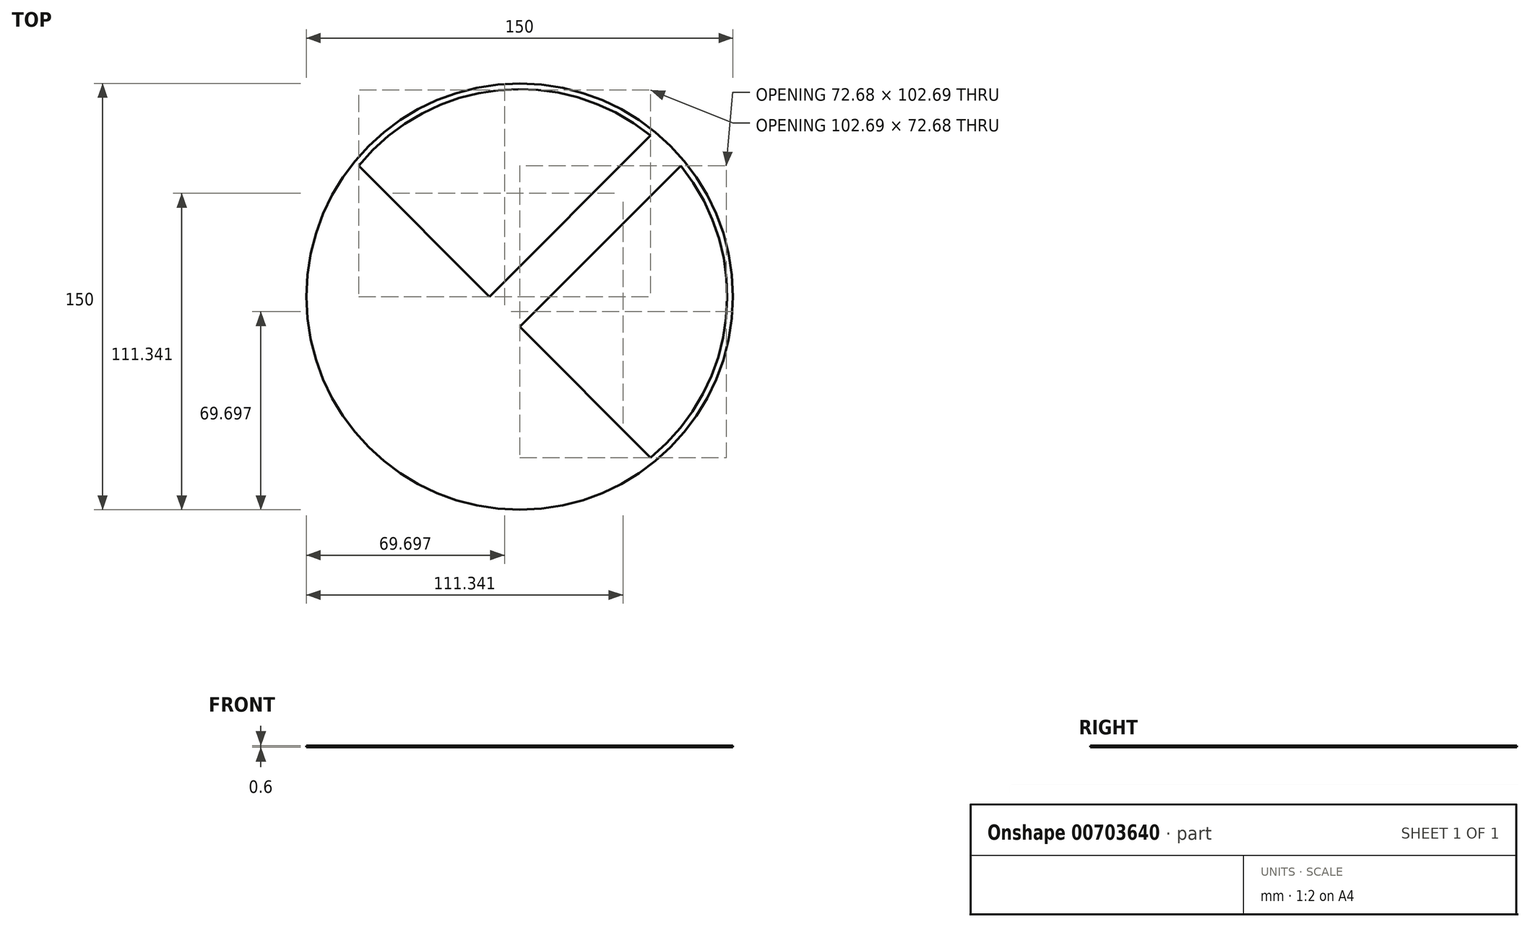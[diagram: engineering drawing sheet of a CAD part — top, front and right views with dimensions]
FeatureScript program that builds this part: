
annotation { "Feature Type Name" : "Feature", "Feature Type Description" : "" }
export const myFeature = defineFeature(function(context is Context, id is Id, definition is map)
    precondition{}
    {
        {
            var Q0;
            Q0=qCreatedBy(makeId("Top.planeOp"),FACE);
            var sketch = newSketch(context, id + "F0", { "sketchPlane" : qUnion([Q0])});
            skCircle(sketch, "E0", {"center": v(0, 0) * mm, "radius": 75 * mm});
            skCircle(sketch, "E1.0", {"center": v(0, 0) * mm, "radius": 73 * mm});
            skLineSegment(sketch, "E2", {"start": v(-56.65, 46.04) * mm, "end": v(46.04, -56.65) * mm});
            skLineSegment(sketch, "E3", {"start": v(46.04, -56.65) * mm, "end": v(45.52, -55.64) * mm});
            skLineSegment(sketch, "E4", {"start": v(56.65, 46.04) * mm, "end": v(-46.04, -56.65) * mm});
            skLineSegment(sketch, "E5", {"start": v(-56.65, -46.04) * mm, "end": v(46.04, 56.65) * mm});
            skLineSegment(sketch, "E6", {"start": v(-46.04, 56.65) * mm, "end": v(56.65, -46.04) * mm});
            skSolve(sketch);
        }
        {
            var Q0;
            Q0=makeQuery(id+"F0.imprint","IMPRINT",FACE,{"disambiguationData":[TD([[makeQuery(id+"F0.imprint","IMPRINT",EDGE,{"derivedFrom":sQuery(id+"F0.wireOp",EDGE,"E0")}),1.0]])]});
            var Q1;
            {var subQ0=sQuery(id+"F0.wireOp",EDGE,"E2");var subQ1=sQuery(id+"F0.wireOp",EDGE,"E1.0");var subQ2=makeQuery(id+"F0.imprint","INTERSECT",VERTEX,{"disambiguationData":[OD(0.0)],"derivedFrom":[subQ1,subQ0]});Q1=makeQuery(id+"F0.imprint","IMPRINT",FACE,{"disambiguationData":[TD([[makeQuery(id+"F0.imprint","IMPRINT",EDGE,{"disambiguationData":[TD([[subQ2,1.0]])],"derivedFrom":subQ1}),1.0]])]});}
            var Q2;
            {var subQ0=sQuery(id+"F0.wireOp",EDGE,"E4");var subQ1=sQuery(id+"F0.wireOp",EDGE,"E1.0");var subQ2=makeQuery(id+"F0.imprint","INTERSECT",VERTEX,{"disambiguationData":[OD(1.0)],"derivedFrom":[subQ1,subQ0]});Q2=makeQuery(id+"F0.imprint","IMPRINT",FACE,{"disambiguationData":[TD([[makeQuery(id+"F0.imprint","IMPRINT",EDGE,{"disambiguationData":[TD([[subQ2,1.0]])],"derivedFrom":subQ1}),1.0]])]});}
            var Q3;
            {var subQ0=sQuery(id+"F0.wireOp",EDGE,"E2");var subQ1=sQuery(id+"F0.wireOp",EDGE,"E1.0");var subQ2=makeQuery(id+"F0.imprint","INTERSECT",VERTEX,{"disambiguationData":[OD(1.0)],"derivedFrom":[subQ1,subQ0]});Q3=makeQuery(id+"F0.imprint","IMPRINT",FACE,{"disambiguationData":[TD([[makeQuery(id+"F0.imprint","IMPRINT",EDGE,{"disambiguationData":[TD([[subQ2,-1.0]])],"derivedFrom":subQ1}),1.0]])]});}
            var Q4;
            {var subQ0=sQuery(id+"F0.wireOp",EDGE,"E4");var subQ1=sQuery(id+"F0.wireOp",EDGE,"E1.0");var subQ2=makeQuery(id+"F0.imprint","INTERSECT",VERTEX,{"disambiguationData":[OD(0.0)],"derivedFrom":[subQ1,subQ0]});Q4=makeQuery(id+"F0.imprint","IMPRINT",FACE,{"disambiguationData":[TD([[makeQuery(id+"F0.imprint","IMPRINT",EDGE,{"disambiguationData":[TD([[subQ2,-1.0]])],"derivedFrom":subQ1}),1.0]])]});}
            var Q5;
            {var subQ0=sQuery(id+"F0.wireOp",EDGE,"E5");var subQ1=sQuery(id+"F0.wireOp",EDGE,"E2");var subQ2=makeQuery(id+"F0.imprint","INTERSECT",VERTEX,{"derivedFrom":[subQ1,subQ0]});Q5=makeQuery(id+"F0.imprint","IMPRINT",FACE,{"disambiguationData":[TD([[makeQuery(id+"F0.imprint","IMPRINT",EDGE,{"disambiguationData":[TD([[subQ2,-1.0]])],"derivedFrom":subQ1}),1.0]])]});}
            extrude(context, id + "F1", {"entities" : qUnion([Q0, Q1, Q2, Q3, Q4, Q5]), "depth" : .6 * mm, "offsetDistance" : 25.4 * mm});
        }
    });
